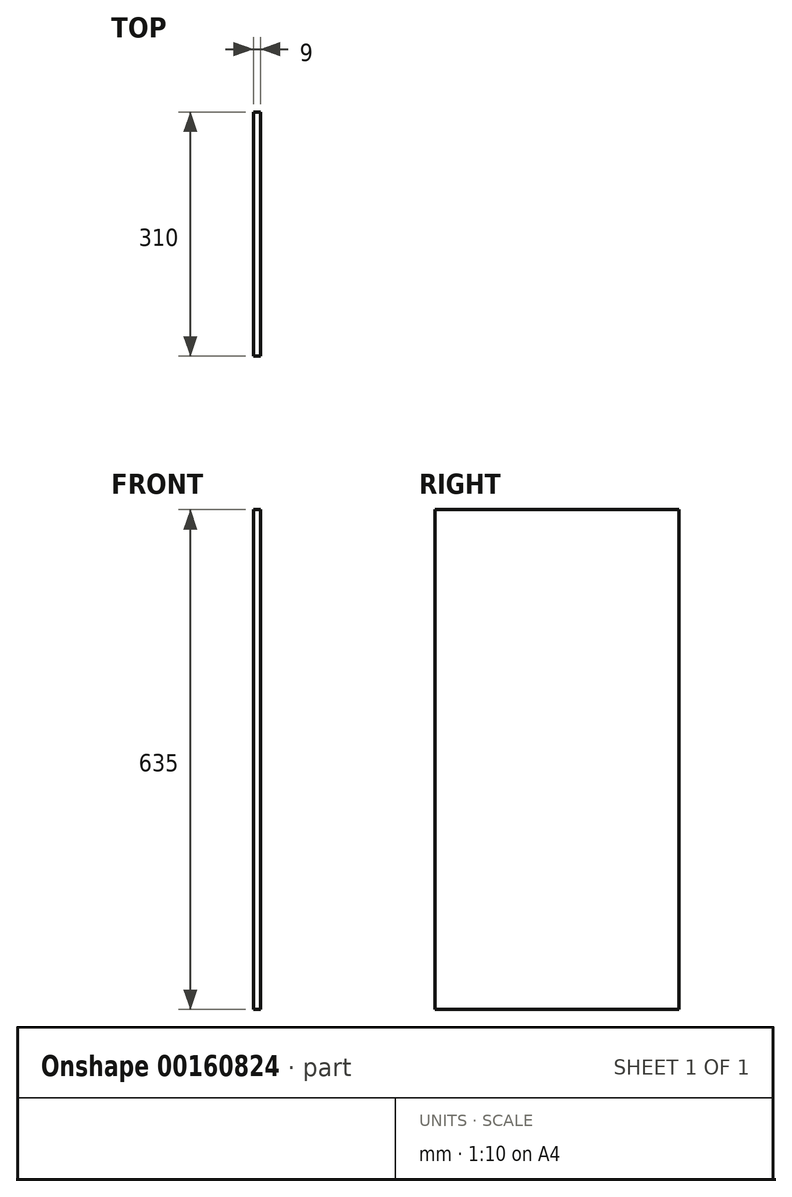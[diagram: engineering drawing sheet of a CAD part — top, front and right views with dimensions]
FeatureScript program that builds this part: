
annotation { "Feature Type Name" : "Feature", "Feature Type Description" : "" }
export const myFeature = defineFeature(function(context is Context, id is Id, definition is map)
    precondition{}
    {
        {
            var Q0;
            Q0=qCreatedBy(makeId("Right.planeOp"),FACE);
            var sketch = newSketch(context, id + "F0", { "sketchPlane" : qUnion([Q0])});
            skLineSegment(sketch, "E0.bottom", {"start": v(0, 0) * mm, "end": v(-310, 0) * mm});
            skLineSegment(sketch, "E0.top", {"start": v(0, 635) * mm, "end": v(-310, 635) * mm});
            skLineSegment(sketch, "E0.left", {"start": v(0, 0) * mm, "end": v(0, 635) * mm});
            skLineSegment(sketch, "E0.right", {"start": v(-310, 0) * mm, "end": v(-310, 635) * mm});
            skSolve(sketch);
        }
        {
            var Q0;
            Q0=makeQuery(id+"F0.imprint","IMPRINT",FACE,{"disambiguationData":[TD([[makeQuery(id+"F0.imprint","IMPRINT",EDGE,{"derivedFrom":sQuery(id+"F0.wireOp",EDGE,"E0.bottom")}),-1.0]])]});
            extrude(context, id + "F1", {"entities" : qUnion([Q0]), "depth" : 9 * mm});
        }
    });
